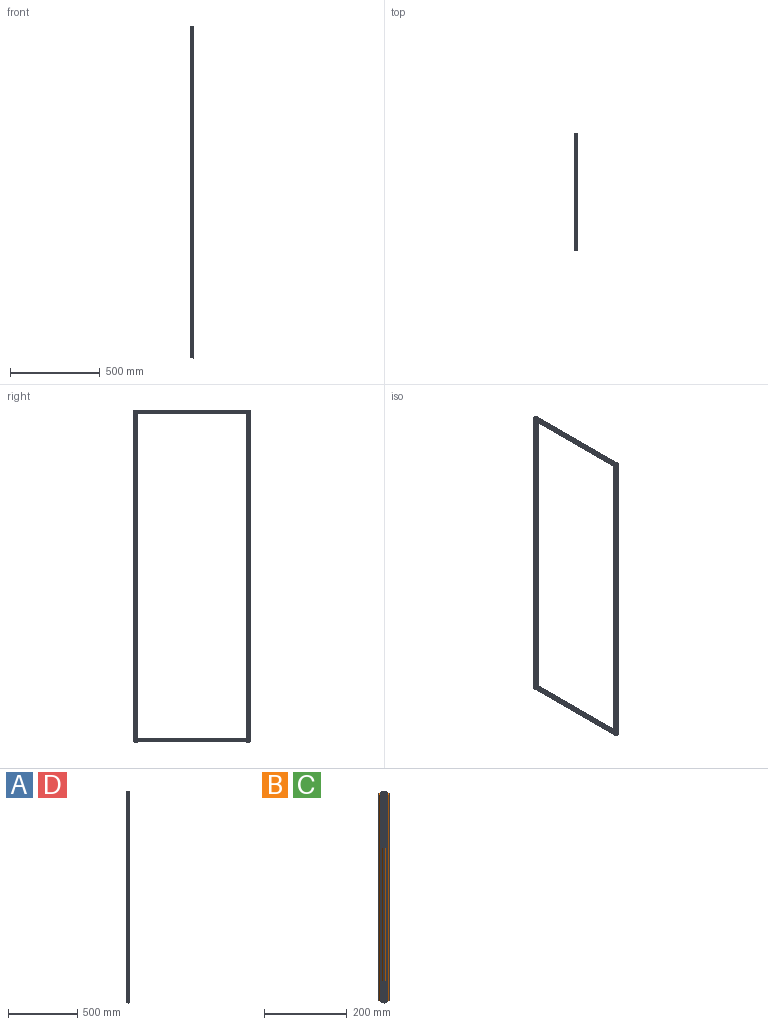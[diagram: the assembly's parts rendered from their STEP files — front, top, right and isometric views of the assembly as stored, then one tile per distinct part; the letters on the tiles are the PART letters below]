
ASSEMBLY  parts=4 mates=9
PART A: 150 faces, bbox 20x20x1854.2 mm
  f0: extruded ~622.3x0.84mm, area 819.3mm2, adj f37,f38,f108,f109
  f1: extruded ~622.3x0.31mm, area 297.9mm2, adj f38,f106,f107,f108
  f2: extruded ~622.3x0.79mm, area 769.7mm2, adj f38,f104,f105,f106
  f3: extruded ~622.3x2.01mm, area 1961.8mm2, adj f38,f102,f103,f104
  f4: extruded ~622.3x0.79mm, area 769.7mm2, adj f38,f100,f101,f102
  f5: extruded ~622.3x0.31mm, area 297.9mm2, adj f38,f98,f99,f100
  f6: extruded ~622.3x1.43mm, area 1229.1mm2, adj f38,f96,f97,f98
  f7: extruded ~622.3x2.12mm, area 1465mm2, adj f38,f94,f95,f96
  f8: extruded ~622.3x2.12mm, area 1465mm2, adj f38,f92,f93,f94
  f9: extruded ~622.3x1.43mm, area 1229.1mm2, adj f38,f90,f91,f92
  f10: extruded ~622.3x0.31mm, area 297.9mm2, adj f38,f88,f89,f90
  f11: extruded ~622.3x0.79mm, area 769.7mm2, adj f38,f86,f87,f88
  f12: extruded ~622.3x2.01mm, area 1961.8mm2, adj f38,f84,f85,f86
  f13: extruded ~622.3x0.79mm, area 769.7mm2, adj f38,f82,f83,f84
  f14: extruded ~622.3x0.31mm, area 297.9mm2, adj f38,f80,f81,f82
  f15: extruded ~622.3x0.84mm, area 819.3mm2, adj f16,f38,f79,f80
  f16: extruded ~622.3x0.59mm, area 409.7mm2, adj f15,f38,f78,f79
  f17: extruded ~622.3x2.12mm, area 1465mm2, adj f38,f76,f77,f78
  f18: extruded ~622.3x2.12mm, area 1465mm2, adj f38,f74,f75,f76
  f19: extruded ~622.3x1.43mm, area 1229.1mm2, adj f38,f72,f73,f74
  f20: extruded ~622.3x0.31mm, area 297.9mm2, adj f38,f70,f71,f72
  f21: extruded ~622.3x0.79mm, area 769.7mm2, adj f38,f68,f69,f70
  f22: extruded ~622.3x2.01mm, area 1961.8mm2, adj f38,f66,f67,f68
  f23: extruded ~622.3x0.79mm, area 769.7mm2, adj f38,f64,f65,f66
  f24: extruded ~622.3x0.31mm, area 297.9mm2, adj f38,f62,f63,f64
  f25: extruded ~622.3x1.43mm, area 1229.1mm2, adj f38,f60,f61,f62
  f26: extruded ~622.3x2.12mm, area 1465mm2, adj f38,f58,f59,f60
  f27: extruded ~622.3x2.12mm, area 1465mm2, adj f38,f56,f57,f58
  f28: extruded ~622.3x1.43mm, area 1229.1mm2, adj f38,f54,f55,f56
  f29: extruded ~622.3x0.31mm, area 297.9mm2, adj f38,f52,f53,f54
  f30: extruded ~622.3x0.79mm, area 769.7mm2, adj f38,f50,f51,f52
  f31: extruded ~622.3x2.01mm, area 1961.8mm2, adj f38,f48,f49,f50
  f32: extruded ~622.3x0.79mm, area 769.7mm2, adj f38,f46,f47,f48
  f33: extruded ~622.3x0.31mm, area 297.9mm2, adj f38,f44,f45,f46
  f34: extruded ~622.3x1.43mm, area 1229.1mm2, adj f38,f42,f43,f44
  f35: extruded ~622.3x2.12mm, area 1465mm2, adj f38,f40,f41,f42
  f36: extruded ~622.3x2.12mm, area 1465mm2, adj f38,f39,f40,f110
  f37: extruded ~622.3x0.59mm, area 409.7mm2, adj f0,f38,f109,f110
  f38: plane 19.99x19.99mm, normal (0,0,-1), area 197.3mm2, adj f0,f1,f2,f3,f4,f5,f6,f7
  f39: revolved ~609.6x2.12mm, area 1435mm2, adj f36,f40,f110,f112
  f40: plane 1854.2x2.27mm, normal (0,1,0), area 4203.2mm2, adj f35,f36,f38,f39,f41,f111,f112,f149
  f41: revolved ~609.6x2.12mm, area 1435mm2, adj f35,f40,f42,f149
  f42: plane 1854.2x2.26mm, normal (-0.71,0.71,0), area 5912.7mm2, adj f34,f35,f38,f41,f43,f111,f148,f149
  f43: revolved ~609.6x1.43mm, area 1203.9mm2, adj f34,f42,f44,f148
  f44: plane 1854.2x2.11mm, normal (0,-1,0), area 3909mm2, adj f33,f34,f38,f43,f45,f111,f147,f148
  f45: revolved ~609.6x0.31mm, area 291.9mm2, adj f33,f44,f46,f147
  f46: plane 1854.2x0.71mm, normal (-1,0,0), area 1318.7mm2, adj f32,f33,f38,f45,f47,f111,f146,f147
  f47: revolved ~609.6x0.79mm, area 754mm2, adj f32,f46,f48,f146
  f48: plane 1854.2x4.7mm, normal (0,1,0), area 8712.9mm2, adj f31,f32,f38,f47,f49,f111,f145,f146
  f49: revolved ~609.6x2.01mm, area 1921.4mm2, adj f31,f48,f50,f145
  f50: plane 1854.2x4.7mm, normal (1,0,0), area 8712.9mm2, adj f30,f31,f38,f49,f51,f111,f144,f145
  f51: revolved ~609.6x0.79mm, area 754mm2, adj f30,f50,f52,f144
  f52: plane 1854.2x0.71mm, normal (0,-1,0), area 1318.7mm2, adj f29,f30,f38,f51,f53,f111,f143,f144
  f53: revolved ~609.6x0.31mm, area 291.9mm2, adj f29,f52,f54,f143
  f54: plane 1854.2x2.11mm, normal (-1,0,0), area 3909mm2, adj f28,f29,f38,f53,f55,f111,f142,f143
  f55: revolved ~609.6x1.43mm, area 1203.9mm2, adj f28,f54,f56,f142
  f56: plane 1854.2x2.26mm, normal (0.71,-0.71,0), area 5912.7mm2, adj f27,f28,f38,f55,f57,f111,f141,f142
  f57: revolved ~609.6x2.12mm, area 1435mm2, adj f27,f56,f58,f141
  f58: plane 1854.2x2.27mm, normal (1,0,0), area 4203.2mm2, adj f26,f27,f38,f57,f59,f111,f140,f141
  f59: revolved ~609.6x2.12mm, area 1435mm2, adj f26,f58,f60,f140
  f60: plane 1854.2x2.26mm, normal (0.71,0.71,0), area 5912.7mm2, adj f25,f26,f38,f59,f61,f111,f139,f140
  f61: revolved ~609.6x1.43mm, area 1203.9mm2, adj f25,f60,f62,f139
  f62: plane 1854.2x2.11mm, normal (-1,0,0), area 3909mm2, adj f24,f25,f38,f61,f63,f111,f138,f139
  f63: revolved ~609.6x0.31mm, area 291.9mm2, adj f24,f62,f64,f138
  f64: plane 1854.2x0.71mm, normal (0,1,0), area 1318.7mm2, adj f23,f24,f38,f63,f65,f111,f137,f138
  f65: revolved ~609.6x0.79mm, area 754mm2, adj f23,f64,f66,f137
  f66: plane 1854.2x4.7mm, normal (1,0,0), area 8712.9mm2, adj f22,f23,f38,f65,f67,f111,f136,f137
  f67: revolved ~609.6x2.01mm, area 1921.4mm2, adj f22,f66,f68,f136
  f68: plane 1854.2x4.7mm, normal (0,-1,0), area 8712.9mm2, adj f21,f22,f38,f67,f69,f111,f135,f136
  f69: revolved ~609.6x0.79mm, area 754mm2, adj f21,f68,f70,f135
  f70: plane 1854.2x0.71mm, normal (-1,0,0), area 1318.7mm2, adj f20,f21,f38,f69,f71,f111,f134,f135
  f71: revolved ~609.6x0.31mm, area 291.9mm2, adj f20,f70,f72,f134
  f72: plane 1854.2x2.11mm, normal (0,1,0), area 3909mm2, adj f19,f20,f38,f71,f73,f111,f133,f134
  f73: revolved ~609.6x1.43mm, area 1203.9mm2, adj f19,f72,f74,f133
  f74: plane 1854.2x2.26mm, normal (-0.71,-0.71,0), area 5912.7mm2, adj f18,f19,f38,f73,f75,f111,f132,f133
  f75: revolved ~609.6x2.12mm, area 1435mm2, adj f18,f74,f76,f132
  f76: plane 1854.2x2.27mm, normal (0,-1,0), area 4203.2mm2, adj f17,f18,f38,f75,f77,f111,f131,f132
  f77: revolved ~609.6x2.12mm, area 1435mm2, adj f17,f76,f78,f131
  f78: plane 1854.2x2.26mm, normal (0.71,-0.71,0), area 5912.7mm2, adj f16,f17,f38,f77,f79,f111,f129,f131
  f79: revolved ~609.6x1.67mm, area 4414.4mm2, adj f15,f16,f78,f80,f129,f130
  f80: plane 1854.2x2.11mm, normal (0,1,0), area 3909mm2, adj f14,f15,f38,f79,f81,f111,f128,f130
  f81: revolved ~609.6x0.31mm, area 291.9mm2, adj f14,f80,f82,f128
  f82: plane 1854.2x0.71mm, normal (1,0,0), area 1318.7mm2, adj f13,f14,f38,f81,f83,f111,f127,f128
  f83: revolved ~609.6x0.79mm, area 754mm2, adj f13,f82,f84,f127
  f84: plane 1854.2x4.7mm, normal (0,-1,0), area 8712.9mm2, adj f12,f13,f38,f83,f85,f111,f126,f127
  f85: revolved ~609.6x2.01mm, area 1921.4mm2, adj f12,f84,f86,f126
  f86: plane 1854.2x4.7mm, normal (-1,0,0), area 8712.9mm2, adj f11,f12,f38,f85,f87,f111,f125,f126
  f87: revolved ~609.6x0.79mm, area 754mm2, adj f11,f86,f88,f125
  f88: plane 1854.2x0.71mm, normal (0,1,0), area 1318.7mm2, adj f10,f11,f38,f87,f89,f111,f124,f125
  f89: revolved ~609.6x0.31mm, area 291.9mm2, adj f10,f88,f90,f124
  f90: plane 1854.2x2.11mm, normal (1,0,0), area 3909mm2, adj f9,f10,f38,f89,f91,f111,f123,f124
  f91: revolved ~609.6x1.43mm, area 1203.9mm2, adj f9,f90,f92,f123
  f92: plane 1854.2x2.26mm, normal (-0.71,0.71,0), area 5912.7mm2, adj f8,f9,f38,f91,f93,f111,f122,f123
  f93: revolved ~609.6x2.12mm, area 1435mm2, adj f8,f92,f94,f122
  f94: plane 1854.2x2.27mm, normal (-1,0,0), area 4203.2mm2, adj f7,f8,f38,f93,f95,f111,f121,f122
  f95: revolved ~609.6x2.12mm, area 1435mm2, adj f7,f94,f96,f121
  f96: plane 1854.2x2.26mm, normal (-0.71,-0.71,0), area 5912.7mm2, adj f6,f7,f38,f95,f97,f111,f120,f121
  f97: revolved ~609.6x1.43mm, area 1203.9mm2, adj f6,f96,f98,f120
  f98: plane 1854.2x2.11mm, normal (1,0,0), area 3909mm2, adj f5,f6,f38,f97,f99,f111,f119,f120
  f99: revolved ~609.6x0.31mm, area 291.9mm2, adj f5,f98,f100,f119
  f100: plane 1854.2x0.71mm, normal (0,-1,0), area 1318.7mm2, adj f4,f5,f38,f99,f101,f111,f118,f119
  f101: revolved ~609.6x0.79mm, area 754mm2, adj f4,f100,f102,f118
  f102: plane 1854.2x4.7mm, normal (-1,0,0), area 8712.9mm2, adj f3,f4,f38,f101,f103,f111,f117,f118
  f103: revolved ~609.6x2.01mm, area 1921.4mm2, adj f3,f102,f104,f117
  f104: plane 1854.2x4.7mm, normal (0,1,0), area 8712.9mm2, adj f2,f3,f38,f103,f105,f111,f116,f117
  f105: revolved ~609.6x0.79mm, area 754mm2, adj f2,f104,f106,f116
  f106: plane 1854.2x0.71mm, normal (1,0,0), area 1318.7mm2, adj f1,f2,f38,f105,f107,f111,f115,f116
  f107: revolved ~609.6x0.31mm, area 291.9mm2, adj f1,f106,f108,f115
  f108: plane 1854.2x2.11mm, normal (0,-1,0), area 3909mm2, adj f0,f1,f38,f107,f109,f111,f114,f115
  f109: revolved ~609.6x1.67mm, area 4414.4mm2, adj f0,f37,f108,f110,f113,f114
  f110: plane 1854.2x2.26mm, normal (0.71,0.71,0), area 5912.7mm2, adj f36,f37,f38,f39,f109,f111,f112,f113
  f111: plane 19.99x19.99mm, normal (0,0,1), area 197.3mm2, adj f40,f42,f44,f46,f48,f50,f52,f54
  f112: extruded ~622.3x2.12mm, area 1465mm2, adj f39,f40,f110,f111
  f113: extruded ~622.3x0.59mm, area 409.7mm2, adj f109,f110,f111,f114
  f114: extruded ~622.3x0.84mm, area 819.3mm2, adj f108,f109,f111,f113
  f115: extruded ~622.3x0.31mm, area 297.9mm2, adj f106,f107,f108,f111
  f116: extruded ~622.3x0.79mm, area 769.7mm2, adj f104,f105,f106,f111
  f117: extruded ~622.3x2.01mm, area 1961.8mm2, adj f102,f103,f104,f111
  f118: extruded ~622.3x0.79mm, area 769.7mm2, adj f100,f101,f102,f111
  f119: extruded ~622.3x0.31mm, area 297.9mm2, adj f98,f99,f100,f111
  f120: extruded ~622.3x1.43mm, area 1229.1mm2, adj f96,f97,f98,f111
  f121: extruded ~622.3x2.12mm, area 1465mm2, adj f94,f95,f96,f111
  f122: extruded ~622.3x2.12mm, area 1465mm2, adj f92,f93,f94,f111
  f123: extruded ~622.3x1.43mm, area 1229.1mm2, adj f90,f91,f92,f111
  f124: extruded ~622.3x0.31mm, area 297.9mm2, adj f88,f89,f90,f111
  f125: extruded ~622.3x0.79mm, area 769.7mm2, adj f86,f87,f88,f111
  f126: extruded ~622.3x2.01mm, area 1961.8mm2, adj f84,f85,f86,f111
  f127: extruded ~622.3x0.79mm, area 769.7mm2, adj f82,f83,f84,f111
  f128: extruded ~622.3x0.31mm, area 297.9mm2, adj f80,f81,f82,f111
  f129: extruded ~622.3x0.59mm, area 409.7mm2, adj f78,f79,f111,f130
  f130: extruded ~622.3x0.84mm, area 819.3mm2, adj f79,f80,f111,f129
  f131: extruded ~622.3x2.12mm, area 1465mm2, adj f76,f77,f78,f111
  f132: extruded ~622.3x2.12mm, area 1465mm2, adj f74,f75,f76,f111
  f133: extruded ~622.3x1.43mm, area 1229.1mm2, adj f72,f73,f74,f111
  f134: extruded ~622.3x0.31mm, area 297.9mm2, adj f70,f71,f72,f111
  f135: extruded ~622.3x0.79mm, area 769.7mm2, adj f68,f69,f70,f111
  f136: extruded ~622.3x2.01mm, area 1961.8mm2, adj f66,f67,f68,f111
  f137: extruded ~622.3x0.79mm, area 769.7mm2, adj f64,f65,f66,f111
  f138: extruded ~622.3x0.31mm, area 297.9mm2, adj f62,f63,f64,f111
  f139: extruded ~622.3x1.43mm, area 1229.1mm2, adj f60,f61,f62,f111
  f140: extruded ~622.3x2.12mm, area 1465mm2, adj f58,f59,f60,f111
  f141: extruded ~622.3x2.12mm, area 1465mm2, adj f56,f57,f58,f111
  f142: extruded ~622.3x1.43mm, area 1229.1mm2, adj f54,f55,f56,f111
  f143: extruded ~622.3x0.31mm, area 297.9mm2, adj f52,f53,f54,f111
  f144: extruded ~622.3x0.79mm, area 769.7mm2, adj f50,f51,f52,f111
  f145: extruded ~622.3x2.01mm, area 1961.8mm2, adj f48,f49,f50,f111
  f146: extruded ~622.3x0.79mm, area 769.7mm2, adj f46,f47,f48,f111
  f147: extruded ~622.3x0.31mm, area 297.9mm2, adj f44,f45,f46,f111
  f148: extruded ~622.3x1.43mm, area 1229.1mm2, adj f42,f43,f44,f111
  f149: extruded ~622.3x2.12mm, area 1465mm2, adj f40,f41,f42,f111
PART B: 78 faces, bbox 20x20x609.6 mm
  f0: revolved ~40.33x4.29mm, area 543.8mm2, adj f74,f76
  f1: revolved ~609.6x2.12mm, area 1435mm2, adj f2,f72,f73,f74
  f2: plane 609.6x2.27mm, normal (0,1,0), area 1381.9mm2, adj f1,f3,f73,f74
  f3: revolved ~609.6x2.12mm, area 1435mm2, adj f2,f4,f73,f74
  f4: plane 609.6x2.26mm, normal (-0.71,0.71,0), area 1943.9mm2, adj f3,f5,f73,f74
  f5: revolved ~609.6x1.43mm, area 1203.9mm2, adj f4,f6,f73,f74
  f6: plane 609.6x2.11mm, normal (0,-1,0), area 1285.2mm2, adj f5,f7,f73,f74
  f7: revolved ~609.6x0.31mm, area 291.9mm2, adj f6,f8,f73,f74
  f8: plane 609.6x0.71mm, normal (-1,0,0), area 433.5mm2, adj f7,f9,f73,f74
  f9: revolved ~609.6x0.79mm, area 754mm2, adj f8,f10,f73,f74
  f10: plane 609.6x4.7mm, normal (0,1,0), area 2864.5mm2, adj f9,f11,f73,f74
  f11: revolved ~609.6x2.01mm, area 1921.4mm2, adj f10,f12,f73,f74
  f12: plane 609.6x4.7mm, normal (1,0,0), area 2864.5mm2, adj f11,f13,f73,f74
  f13: revolved ~609.6x0.79mm, area 754mm2, adj f12,f14,f73,f74
  f14: plane 609.6x0.71mm, normal (0,-1,0), area 433.5mm2, adj f13,f15,f73,f74
  f15: revolved ~609.6x0.31mm, area 291.9mm2, adj f14,f16,f73,f74
  f16: plane 609.6x2.11mm, normal (-1,0,0), area 1285.2mm2, adj f15,f17,f73,f74
  f17: revolved ~609.6x1.43mm, area 1203.9mm2, adj f16,f18,f73,f74
  f18: plane 609.6x2.26mm, normal (0.71,-0.71,0), area 1943.9mm2, adj f17,f19,f73,f74
  f19: revolved ~609.6x2.12mm, area 1435mm2, adj f18,f20,f73,f74
  f20: plane 609.6x2.27mm, normal (1,0,0), area 1381.9mm2, adj f19,f21,f73,f74
  f21: revolved ~609.6x2.12mm, area 1435mm2, adj f20,f22,f73,f74
  f22: plane 609.6x2.26mm, normal (0.71,0.71,0), area 1943.9mm2, adj f21,f23,f73,f74
  f23: revolved ~609.6x1.43mm, area 1203.9mm2, adj f22,f24,f73,f74
  f24: plane 609.6x2.11mm, normal (-1,0,0), area 1285.2mm2, adj f23,f25,f73,f74
  f25: revolved ~609.6x0.31mm, area 291.9mm2, adj f24,f26,f73,f74
  f26: plane 609.6x0.71mm, normal (0,1,0), area 433.5mm2, adj f25,f27,f73,f74
  f27: revolved ~609.6x0.79mm, area 754mm2, adj f26,f28,f73,f74
  f28: plane 609.6x4.7mm, normal (1,0,0), area 2864.5mm2, adj f27,f29,f73,f74
  f29: revolved ~609.6x2.01mm, area 1921.4mm2, adj f28,f30,f73,f74
  f30: plane 609.6x4.7mm, normal (0,-1,0), area 2864.5mm2, adj f29,f31,f73,f74
  f31: revolved ~609.6x0.79mm, area 754mm2, adj f30,f32,f73,f74
  f32: plane 609.6x0.71mm, normal (-1,0,0), area 433.5mm2, adj f31,f33,f73,f74
  f33: revolved ~609.6x0.31mm, area 291.9mm2, adj f32,f34,f73,f74
  f34: plane 609.6x2.11mm, normal (0,1,0), area 1285.2mm2, adj f33,f35,f73,f74
  f35: revolved ~609.6x1.43mm, area 1203.9mm2, adj f34,f36,f73,f74
  f36: plane 609.6x2.26mm, normal (-0.71,-0.71,0), area 1943.9mm2, adj f35,f37,f73,f74
  f37: revolved ~609.6x2.12mm, area 1435mm2, adj f36,f38,f73,f74
  f38: plane 609.6x2.27mm, normal (0,-1,0), area 1381.9mm2, adj f37,f39,f73,f74
  f39: revolved ~609.6x2.12mm, area 1435mm2, adj f38,f40,f73,f74
  f40: plane 609.6x2.26mm, normal (0.71,-0.71,0), area 1943.9mm2, adj f39,f41,f73,f74
  f41: revolved ~609.6x1.43mm, area 1203.9mm2, adj f40,f42,f73,f74
  f42: plane 609.6x2.11mm, normal (0,1,0), area 1285.2mm2, adj f41,f43,f73,f74
  f43: revolved ~609.6x0.31mm, area 291.9mm2, adj f42,f44,f73,f74
  f44: plane 609.6x0.71mm, normal (1,0,0), area 433.5mm2, adj f43,f45,f73,f74
  f45: revolved ~609.6x0.79mm, area 754mm2, adj f44,f46,f73,f74
  f46: plane 609.6x4.7mm, normal (0,-1,0), area 2864.5mm2, adj f45,f47,f73,f74
  f47: revolved ~609.6x2.01mm, area 1921.4mm2, adj f46,f48,f73,f74
  f48: plane 609.6x4.7mm, normal (-1,0,0), area 2864.5mm2, adj f47,f49,f73,f74
  f49: revolved ~609.6x0.79mm, area 754mm2, adj f48,f50,f73,f74
  f50: plane 609.6x0.71mm, normal (0,1,0), area 433.5mm2, adj f49,f51,f73,f74
  f51: revolved ~609.6x0.31mm, area 291.9mm2, adj f50,f52,f73,f74
  f52: plane 609.6x2.11mm, normal (1,0,0), area 1285.2mm2, adj f51,f53,f73,f74
  f53: revolved ~609.6x1.43mm, area 1203.9mm2, adj f52,f54,f73,f74
  f54: plane 609.6x2.26mm, normal (-0.71,0.71,0), area 1943.9mm2, adj f53,f55,f73,f74
  f55: revolved ~609.6x2.12mm, area 1435mm2, adj f54,f56,f73,f74
  f56: plane 609.6x2.27mm, normal (-1,0,0), area 1381.9mm2, adj f55,f57,f73,f74
  f57: revolved ~609.6x2.12mm, area 1435mm2, adj f56,f58,f73,f74
  f58: plane 609.6x2.26mm, normal (-0.71,-0.71,0), area 1943.9mm2, adj f57,f59,f73,f74
  f59: revolved ~609.6x1.43mm, area 1203.9mm2, adj f58,f60,f73,f74
  f60: plane 609.6x2.11mm, normal (1,0,0), area 1285.2mm2, adj f59,f61,f73,f74
  f61: revolved ~609.6x0.31mm, area 291.9mm2, adj f60,f62,f73,f74
  f62: plane 609.6x0.71mm, normal (0,-1,0), area 433.5mm2, adj f61,f63,f73,f74
  f63: revolved ~609.6x0.79mm, area 754mm2, adj f62,f64,f73,f74
  f64: plane 609.6x4.7mm, normal (-1,0,0), area 2864.5mm2, adj f63,f65,f73,f74
  f65: revolved ~609.6x2.01mm, area 1921.4mm2, adj f64,f66,f73,f74
  f66: plane 609.6x4.7mm, normal (0,1,0), area 2864.5mm2, adj f65,f67,f73,f74
  f67: revolved ~609.6x0.79mm, area 754mm2, adj f66,f68,f73,f74
  f68: plane 609.6x0.71mm, normal (1,0,0), area 433.5mm2, adj f67,f69,f73,f74
  f69: revolved ~609.6x0.31mm, area 291.9mm2, adj f68,f70,f73,f74
  f70: plane 609.6x2.11mm, normal (0,-1,0), area 1285.2mm2, adj f69,f71,f73,f74
  f71: revolved ~609.6x1.67mm, area 4414.4mm2, adj f70,f72,f73,f74
  f72: plane 609.6x2.26mm, normal (0.71,0.71,0), area 1943.9mm2, adj f1,f71,f73,f74
  f73: plane 19.99x19.99mm, normal (0,0,1), area 182.8mm2, adj f1,f2,f3,f4,f5,f6,f7,f8
  f74: plane 19.99x19.99mm, normal (0,0,-1), area 182.8mm2, adj f0,f1,f2,f3,f4,f5,f6,f7
  f75: revolved ~80.33x4.29mm, area 1083.2mm2, adj f73,f77
  f76: plane 4.29x4.29mm, normal (0,0,-1), area 14.5mm2, adj f0
  f77: plane 4.29x4.29mm, normal (0,0,1), area 14.5mm2, adj f75
PART C: same geometry as B
PART D: same geometry as A
PLACE A t=(502.79,-58.51,-639.58)mm
PLACE B rot(axis=(1,0,0),90deg) t=(502.79,256.29,277.52)mm
PLACE C rot(axis=(1,0,0),90deg) t=(502.79,256.29,-1556.69)mm
PLACE D t=(502.79,571.08,-639.58)mm fixed
MATE planar C.f46 <-> D.f38  axis (0,0,-1) through (497.15,356.29,-1566.68)mm
MATE planar A.f38 <-> D.f38  axis (0,0,-1) through (502.79,-58.51,-1566.68)mm
MATE planar A.f50 <-> B.f12  axis (1,0,0) through (512.79,-52.87,-176.03)mm
MATE planar B.f74 <-> D.f84  axis (0,1,0) through (502.79,561.09,277.52)mm
MATE planar C.f64 <-> D.f86  axis (-1,0,0) through (492.8,256.29,-1551.05)mm
MATE planar A.f50 <-> D.f50  axis (1,0,0) through (512.79,-52.87,-176.03)mm
MATE planar B.f10 <-> A.f111  axis (0,0,1) through (508.43,256.29,287.52)mm
MATE planar C.f74 <-> D.f84  axis (0,1,0) through (502.79,561.09,-1556.69)mm
MATE planar C.f73 <-> A.f48  axis (0,-1,0) through (502.79,-48.51,-1556.69)mm
